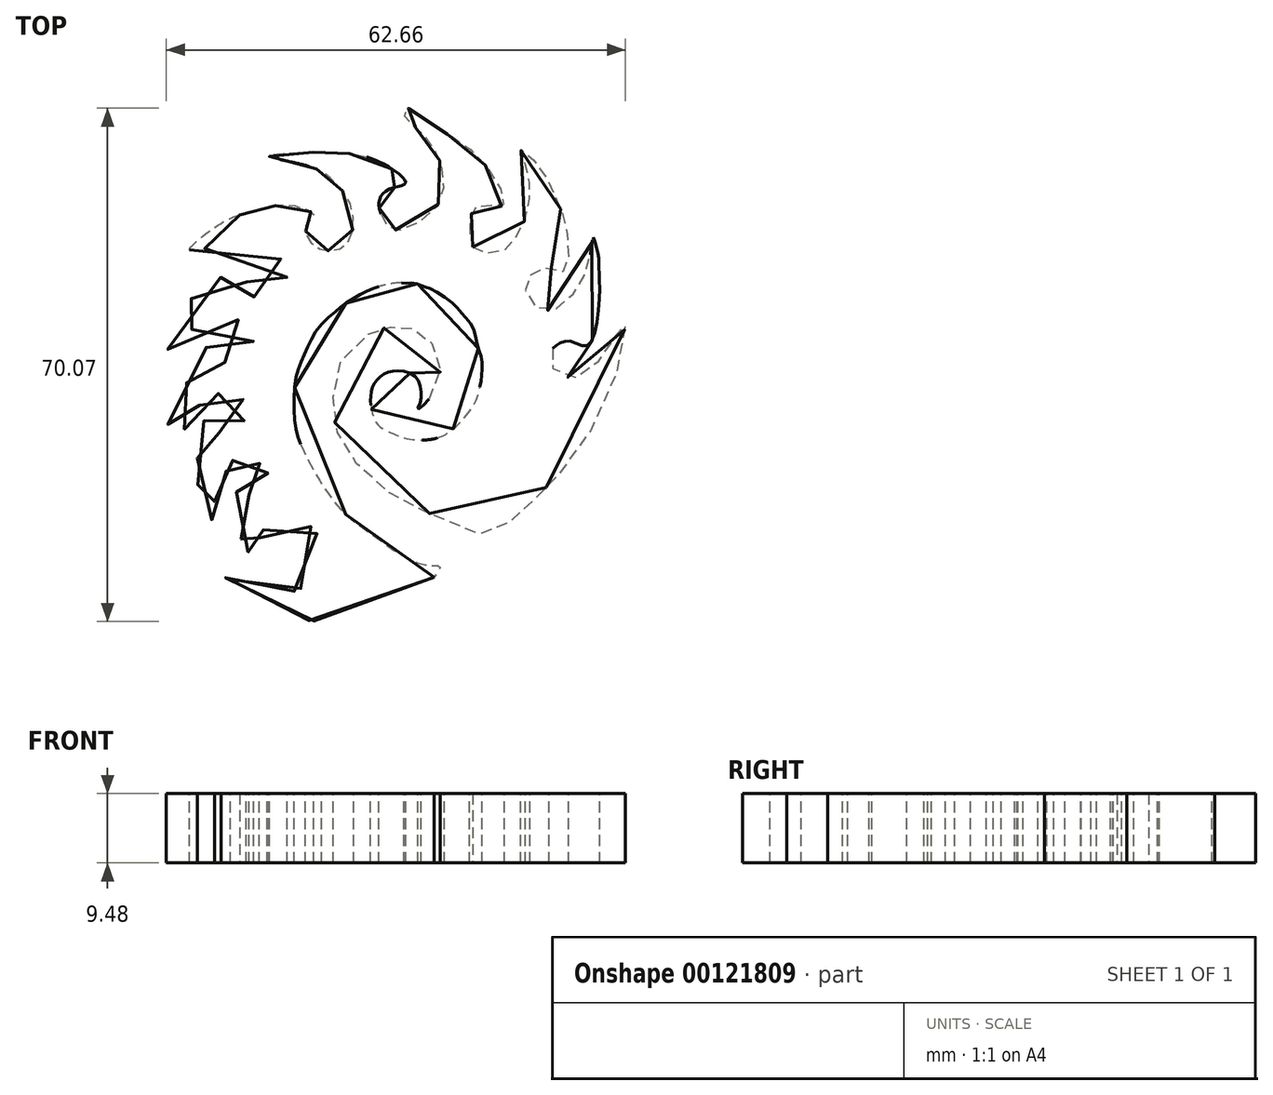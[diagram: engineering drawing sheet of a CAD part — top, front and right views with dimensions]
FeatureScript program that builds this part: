
annotation { "Feature Type Name" : "Feature", "Feature Type Description" : "" }
export const myFeature = defineFeature(function(context is Context, id is Id, definition is map)
    precondition{}
    {
        {
            var Q0;
            Q0=qCreatedBy(makeId("Top.planeOp"),FACE);
            var sketch = newSketch(context, id + "F0", { "sketchPlane" : qUnion([Q0])});
            skFitSpline(sketch, "E0", {"points": [v(-75.98, 0) * mm, v(-85.3, -5.38) * mm, v(-100.67, -3.85) * mm, v(-105.02, 0) * mm, v(-101.3, -1.52) * mm, v(-98.19, -2.3) * mm, v(-95.24, -1.98) * mm, v(-92.29, 0) * mm, v(-91.35, 3.45) * mm, v(-92.44, 6.56) * mm, v(-96.01, 8.27) * mm, v(-98.34, 7.8) * mm, v(-99.43, 6.1) * mm, v(-99.74, 4.23) * mm, v(-98.81, 2.06) * mm, v(-100.83, 2.83) * mm, v(-102.7, 6.1) * mm, v(-103.78, 9.2) * mm, v(-103.16, 11.53) * mm, v(-101.14, 11.22) * mm, v(-99.43, 11.84) * mm, v(-98.66, 12.77) * mm, v(-98.5, 13.86) * mm, v(-99.43, 15.1) * mm, v(-100.36, 16.04) * mm, v(-101.92, 16.2) * mm, v(-103, 16.35) * mm, v(-103.63, 15.73) * mm, v(-104.25, 14.64) * mm, v(-105.02, 13.55) * mm, v(-105.96, 11.38) * mm, v(-105.96, 10.29) * mm, v(-106.27, 7.96) * mm, v(-106.58, 7.65) * mm, v(-107.82, 9.82) * mm, v(-108.29, 14.33) * mm, v(-108.29, 18.21) * mm, v(-107.66, 21.63) * mm, v(-106.42, 19.92) * mm, v(-105.18, 19.76) * mm, v(-103.63, 19.76) * mm, v(-102.07, 21) * mm, v(-101.6, 22.87) * mm, v(-102.23, 24.42) * mm, v(-103.63, 24.73) * mm, v(-105.18, 25.04) * mm, v(-106.58, 24.89) * mm, v(-107.97, 23.5) * mm, v(-109.37, 21.63) * mm, v(-110.3, 19.92) * mm, v(-112.44, 19.45) * mm, v(-110.46, 24.73) * mm, v(-109.22, 28.15) * mm, v(-106.89, 31.41) * mm, v(-105.49, 29.86) * mm, v(-103.16, 29.4) * mm, v(-100.67, 31.88) * mm, v(-101.76, 34.52) * mm, v(-104.56, 35.45) * mm, v(-109.84, 33.28) * mm, v(-112.44, 31.1) * mm, v(-110.3, 36.54) * mm, v(-104.56, 41.2) * mm, v(-101.3, 42.13) * mm, v(-101.6, 40.11) * mm, v(-100.83, 38.4) * mm, v(-97.72, 38.25) * mm, v(-96.17, 40.27) * mm, v(-96.64, 43.06) * mm, v(-102.38, 45.7) * mm, v(-109.37, 44.62) * mm, v(-105.02, 48.34) * mm, v(-102.52, 49.42) * mm], "startDerivative": vector(-300.45, -240.3) * mm, "endDerivative": vector(145.06, 38.75) * mm});
            skFitSpline(sketch, "E1", {"points": [v(-102.52, 49.42) * mm, v(-98.5, 50.57) * mm, v(-95.02, 50.7) * mm, v(-92.4, 49.42) * mm, v(-93.32, 48.35) * mm, v(-93.06, 46) * mm, v(-90.58, 44.56) * mm, v(-87.7, 45.73) * mm, v(-87.31, 50.7) * mm, v(-89.53, 53.83) * mm, v(-92.54, 55.92) * mm, v(-98.5, 57.5) * mm, v(-91.89, 58.01) * mm, v(-88.23, 57.88) * mm, v(-83.79, 56.84) * mm, v(-79.87, 53.83) * mm, v(-82.22, 52.92) * mm, v(-83.53, 51.1) * mm, v(-83.13, 49.42) * mm, v(-81.57, 47.43) * mm, v(-75.56, 50.7) * mm, v(-75.04, 56.32) * mm, v(-77.65, 60.63) * mm, v(-80, 62.98) * mm, v(-79.74, 64) * mm, v(-75.17, 61.15) * mm, v(-69.68, 57.1) * mm, v(-66.55, 50.83) * mm, v(-69.94, 50.7) * mm, v(-71.12, 48.22) * mm, v(-70.73, 45.08) * mm], "startDerivative": vector(118.02, 36.9) * mm, "endDerivative": vector(20.63, -98.8) * mm});
            skFitSpline(sketch, "E2", {"points": [v(-70.73, 45.08) * mm, v(-69.99, 44.6) * mm, v(-69.33, 44.36) * mm, v(-68.11, 44.2) * mm, v(-66.7, 44.51) * mm, v(-65.59, 45.08) * mm, v(-65.07, 45.97) * mm, v(-64.08, 47.56) * mm, v(-63.58, 48.78) * mm, v(-63.1, 50.78) * mm, v(-62.89, 52) * mm, v(-62.89, 53.13) * mm, v(-62.96, 54.1) * mm, v(-63.22, 55.49) * mm, v(-63.62, 56.7) * mm, v(-64.03, 57.95) * mm, v(-64.13, 58.38) * mm, v(-63.61, 58.08) * mm, v(-62.74, 57.29) * mm, v(-61.47, 55.84) * mm, v(-60.63, 54.48) * mm, v(-60.15, 53.43) * mm, v(-59.5, 52.08) * mm, v(-58.72, 50.3) * mm, v(-58.2, 48.8) * mm, v(-57.85, 47.31) * mm, v(-57.63, 45.08) * mm, v(-57.67, 43.04) * mm, v(-57.95, 41.57) * mm, v(-58.96, 41.98) * mm, v(-60.33, 42.26) * mm, v(-61.44, 42.04) * mm, v(-62.33, 41.62) * mm, v(-62.97, 41.03) * mm, v(-63.48, 40.06) * mm, v(-63.48, 38.85) * mm, v(-62.79, 37.34) * mm, v(-61.08, 36.48) * mm, v(-59.47, 36.61) * mm, v(-58.12, 37.55) * mm, v(-56.73, 38.97) * mm, v(-55.8, 40.42) * mm, v(-55.07, 42.3) * mm, v(-54.68, 43.93) * mm, v(-54.33, 46.21) * mm, v(-54.25, 46.42) * mm, v(-54.02, 45.72) * mm, v(-53.54, 43.77) * mm, v(-53.47, 42.18) * mm, v(-53.42, 38.05) * mm, v(-54.98, 31.65) * mm, v(-57.22, 32.18) * mm, v(-58.97, 31.88) * mm, v(-59.97, 30.96) * mm, v(-60.3, 29.82) * mm, v(-59.73, 28.37) * mm, v(-58.24, 27.39) * mm, v(-56, 27.44) * mm, v(-54, 28.86) * mm, v(-52.63, 30.7) * mm, v(-51.05, 33.2) * mm, v(-49.95, 35.16) * mm, v(-50.13, 32.8) * mm, v(-52.14, 24.7) * mm, v(-58.17, 14.97) * mm, v(-60.8, 12.08) * mm, v(-63.17, 9.77) * mm, v(-65.87, 7.34) * mm, v(-67.72, 5.63) * mm, v(-76.22, 8.5) * mm, v(-80.7, 10.6) * mm, v(-85.28, 14.17) * mm, v(-88.23, 17.75) * mm, v(-89.55, 21.1) * mm, v(-89.73, 24.81) * mm, v(-88.96, 28.95) * mm, v(-86.44, 32.17) * mm, v(-83.33, 33.93) * mm, v(-82.74, 34.04) * mm, v(-81.15, 34.25) * mm, v(-80.25, 34.23) * mm, v(-78.3, 33.7) * mm, v(-76.9, 32.7) * mm, v(-75.98, 31.38) * mm, v(-75.22, 29.12) * mm, v(-75.35, 26.6) * mm, v(-77.16, 23.72) * mm, v(-78.19, 22.94) * mm, v(-77.93, 23.72) * mm, v(-77.73, 25.12) * mm, v(-78.07, 26.73) * mm, v(-79.1, 27.8) * mm, v(-80.93, 28.2) * mm, v(-82.07, 28.02) * mm, v(-83, 27.6) * mm, v(-83.75, 26.95) * mm, v(-84.3, 26.16) * mm, v(-84.5, 25.43) * mm, v(-84.63, 24.41) * mm, v(-84.6, 23.43) * mm, v(-83.8, 20.99) * mm, v(-81.75, 19.66) * mm, v(-79.47, 18.87) * mm, v(-76.94, 18.74) * mm, v(-75.01, 19.2) * mm, v(-72.84, 20.66) * mm, v(-71.36, 22.35) * mm, v(-70.2, 24.24) * mm, v(-69.68, 26.15) * mm, v(-69.47, 27.85) * mm, v(-69.49, 29.77) * mm, v(-70.1, 31.78) * mm, v(-70.73, 34.17) * mm, v(-72.07, 35.9) * mm, v(-73.63, 37.56) * mm, v(-76.63, 39.43) * mm, v(-77.45, 39.68) * mm, v(-78.6, 40.11) * mm, v(-79.87, 40.13) * mm, v(-80.88, 40.18) * mm, v(-82.25, 39.98) * mm, v(-83.26, 39.75) * mm, v(-84.5, 39.33) * mm, v(-86.22, 38.5) * mm, v(-88.13, 37.32) * mm, v(-89.53, 36.2) * mm, v(-91.86, 33.86) * mm, v(-93.19, 31.5) * mm, v(-94.21, 29.24) * mm, v(-94.86, 26.96) * mm, v(-95.08, 22.6) * mm, v(-94.67, 19.58) * mm, v(-93.63, 16.89) * mm, v(-89.32, 9.93) * mm, v(-85.16, 6.33) * mm, v(-80.62, 3.14) * mm, v(-76.86, 1.62) * mm, v(-75.16, 1.4) * mm, v(-75.98, 0) * mm], "startDerivative": vector(158.87, -110.37) * mm, "endDerivative": vector(-220.33, -267.87) * mm});
            skSolve(sketch);
        }
        {
            var Q0;
            Q0 = qSketchRegion(id + "F0", true);
            extrude(context, id + "F1", {"entities" : qUnion([Q0]), "depth" : 9.48 * mm});
        }
    });
